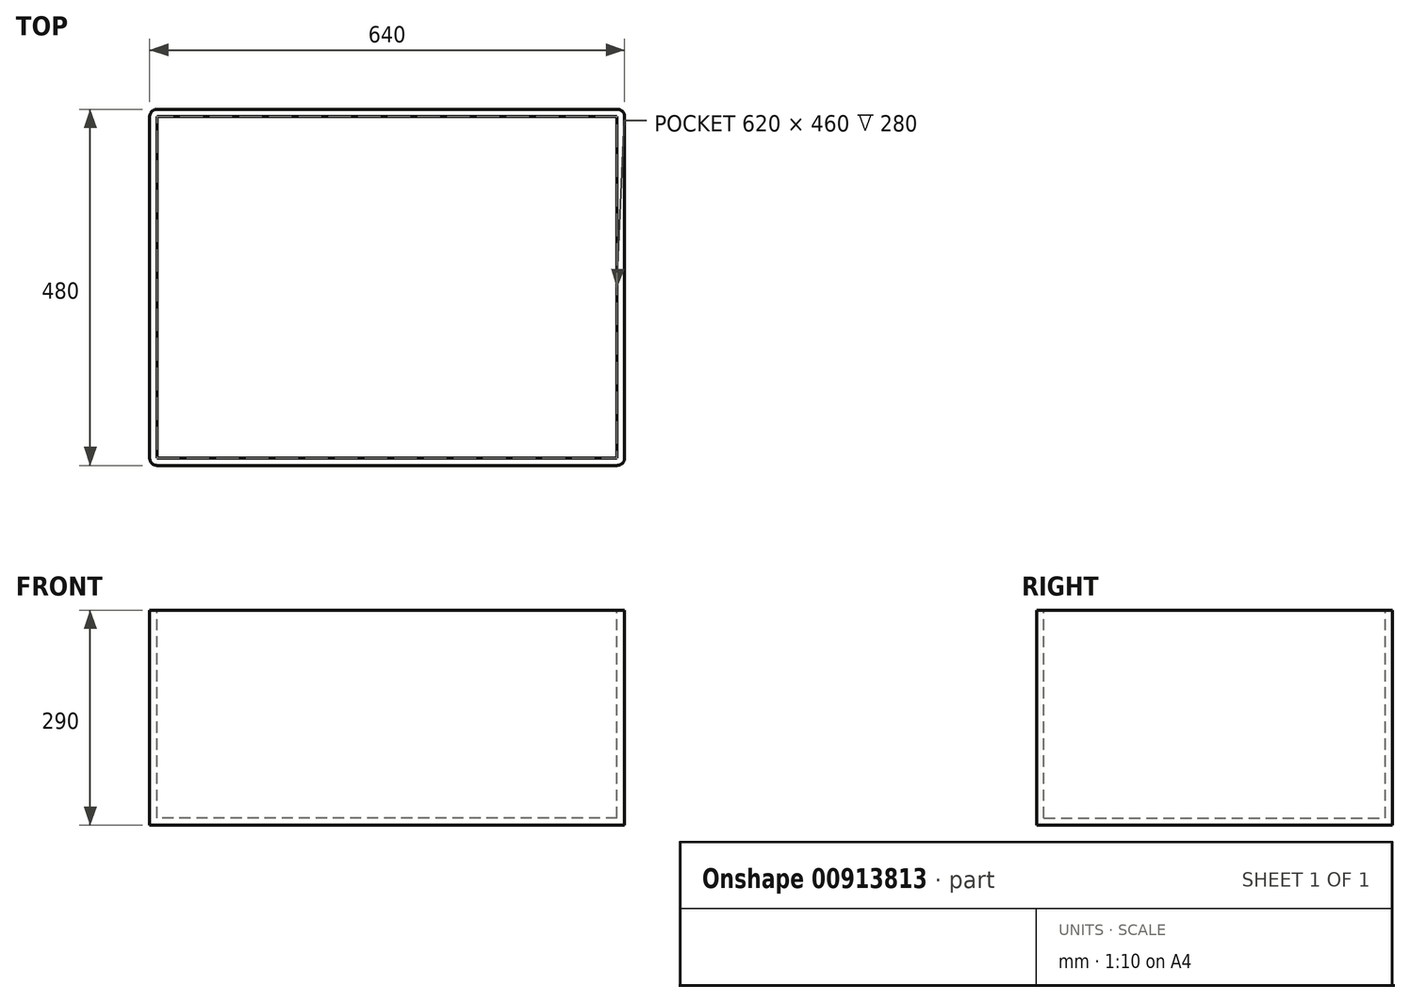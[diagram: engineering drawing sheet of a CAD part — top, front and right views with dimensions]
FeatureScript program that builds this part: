
annotation { "Feature Type Name" : "Feature", "Feature Type Description" : "" }
export const myFeature = defineFeature(function(context is Context, id is Id, definition is map)
    precondition{}
    {
        {
            var Q0;
            Q0=qCreatedBy(makeId("Top.planeOp"),FACE);
            var sketch = newSketch(context, id + "F0", { "sketchPlane" : qUnion([Q0])});
            skLineSegment(sketch, "E0.bottom", {"start": v(310, -230) * mm, "end": v(-310, -230) * mm});
            skLineSegment(sketch, "E0.top", {"start": v(310, 230) * mm, "end": v(-310, 230) * mm});
            skLineSegment(sketch, "E0.left", {"start": v(310, -230) * mm, "end": v(310, 230) * mm});
            skLineSegment(sketch, "E0.right", {"start": v(-310, -230) * mm, "end": v(-310, 230) * mm});
            skPoint(sketch, "E0.middle", {"position": v(0, 0) * mm});
            skLineSegment(sketch, "E1.bottom", {"start": v(320, -240) * mm, "end": v(-320, -240) * mm});
            skLineSegment(sketch, "E1.top", {"start": v(320, 240) * mm, "end": v(-320, 240) * mm});
            skLineSegment(sketch, "E1.left", {"start": v(320, -240) * mm, "end": v(320, 240) * mm});
            skLineSegment(sketch, "E1.right", {"start": v(-320, -240) * mm, "end": v(-320, 240) * mm});
            skSolve(sketch);
        }
        {
            var Q0;
            Q0 = qSketchRegion(id + "F0", true);
            var Q1;
            Q1=makeQuery(id+"F0.imprint","IMPRINT",FACE,{"disambiguationData":[TD([[makeQuery(id+"F0.imprint","IMPRINT",EDGE,{"derivedFrom":sQuery(id+"F0.wireOp",EDGE,"E0.bottom")}),-1.0]])]});
            extrude(context, id + "F1", {"entities" : qUnion([Q0, Q1]), "depth" : -290 * mm, "offsetDistance" : 25 * mm});
        }
        {
            var Q0;
            Q0=makeQuery(id+"F0.imprint","IMPRINT",FACE,{"disambiguationData":[TD([[makeQuery(id+"F0.imprint","IMPRINT",EDGE,{"derivedFrom":sQuery(id+"F0.wireOp",EDGE,"E0.bottom")}),-1.0]])]});
            extrude(context, id + "F2", {"entities" : qUnion([Q0]), "operationType" : NewBodyOperationType.REMOVE, "depth" : -280 * mm, "offsetDistance" : 25 * mm});
        }
        {
            var Q0;
            Q0=makeQuery(id+"F1.opExtrude","SWEPT_EDGE",EDGE,{"disambiguationData":[OSD([sQuery(id+"F0.wireOp",EDGE,"E1.bottom"),sQuery(id+"F0.wireOp",EDGE,"E1.right")])]});
            var Q1;
            Q1=makeQuery(id+"F1.opExtrude","SWEPT_EDGE",EDGE,{"disambiguationData":[OSD([sQuery(id+"F0.wireOp",EDGE,"E1.bottom"),sQuery(id+"F0.wireOp",EDGE,"E1.left")])]});
            var Q2;
            Q2=makeQuery(id+"F1.opExtrude","SWEPT_EDGE",EDGE,{"disambiguationData":[OSD([sQuery(id+"F0.wireOp",EDGE,"E1.top"),sQuery(id+"F0.wireOp",EDGE,"E1.left")])]});
            var Q3;
            Q3=makeQuery(id+"F1.opExtrude","SWEPT_EDGE",EDGE,{"disambiguationData":[OSD([sQuery(id+"F0.wireOp",EDGE,"E1.top"),sQuery(id+"F0.wireOp",EDGE,"E1.right")])]});
            fillet(context, id + "F3", {"entities" : qUnion([Q0, Q1, Q2, Q3]), "radius" : 10 * mm, "tangentPropagation" : true, "allowEdgeOverflow" : false});
        }
    });
